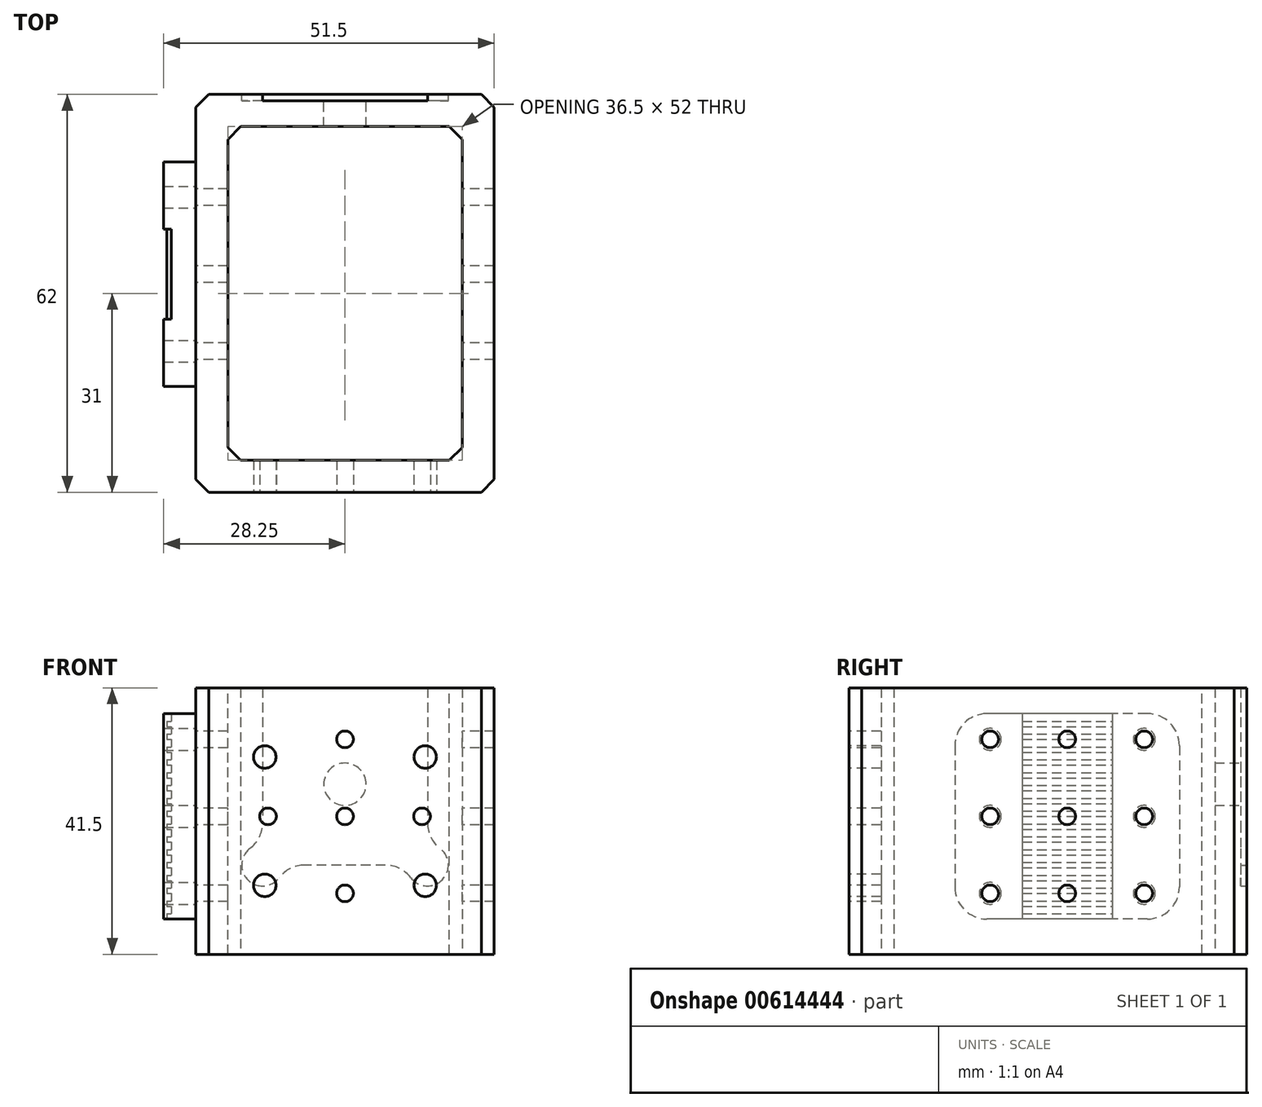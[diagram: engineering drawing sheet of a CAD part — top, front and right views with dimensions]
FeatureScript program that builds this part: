
annotation { "Feature Type Name" : "Feature", "Feature Type Description" : "" }
export const myFeature = defineFeature(function(context is Context, id is Id, definition is map)
    precondition{}
    {
        {
            var Q0;
            Q0=qCreatedBy(makeId("Top.planeOp"),FACE);
            var sketch = newSketch(context, id + "F0", { "sketchPlane" : qUnion([Q0])});
            skLineSegment(sketch, "E0.bottom", {"start": v(-18.25, 26) * mm, "end": v(18.25, 26) * mm});
            skLineSegment(sketch, "E0.top", {"start": v(-18.25, -26) * mm, "end": v(18.25, -26) * mm});
            skLineSegment(sketch, "E0.left", {"start": v(-18.25, 26) * mm, "end": v(-18.25, -26) * mm});
            skLineSegment(sketch, "E0.right", {"start": v(18.25, 26) * mm, "end": v(18.25, -26) * mm});
            skLineSegment(sketch, "E1.0", {"start": v(-23.25, 31) * mm, "end": v(-23.25, -31) * mm});
            skLineSegment(sketch, "E1.1", {"start": v(-23.25, 31) * mm, "end": v(23.25, 31) * mm});
            skLineSegment(sketch, "E1.2", {"start": v(23.25, 31) * mm, "end": v(23.25, -31) * mm});
            skLineSegment(sketch, "E1.3", {"start": v(-23.25, -31) * mm, "end": v(23.25, -31) * mm});
            skSolve(sketch);
        }
        {
            var Q0;
            Q0 = qSketchRegion(id + "F0", true);
            extrude(context, id + "F1", {"entities" : qUnion([Q0]), "depth" : 41.5 * mm, "offsetDistance" : 25 * mm});
        }
        {
            var Q0;
            Q0=makeQuery(id+"F1.opExtrude","SWEPT_EDGE",EDGE,{"disambiguationData":[OSD([sQuery(id+"F0.wireOp",EDGE,"E0.bottom"),sQuery(id+"F0.wireOp",EDGE,"E0.right")])]});
            var Q1;
            Q1=makeQuery(id+"F1.opExtrude","SWEPT_EDGE",EDGE,{"disambiguationData":[OSD([sQuery(id+"F0.wireOp",EDGE,"E0.bottom"),sQuery(id+"F0.wireOp",EDGE,"E0.left")])]});
            var Q2;
            Q2=makeQuery(id+"F1.opExtrude","SWEPT_EDGE",EDGE,{"disambiguationData":[OSD([sQuery(id+"F0.wireOp",EDGE,"E0.top"),sQuery(id+"F0.wireOp",EDGE,"E0.right")])]});
            var Q3;
            Q3=makeQuery(id+"F1.opExtrude","SWEPT_EDGE",EDGE,{"disambiguationData":[OSD([sQuery(id+"F0.wireOp",EDGE,"E0.top"),sQuery(id+"F0.wireOp",EDGE,"E0.left")])]});
            var Q4;
            Q4=makeQuery(id+"F1.opExtrude","SWEPT_EDGE",EDGE,{"disambiguationData":[OSD([sQuery(id+"F0.wireOp",EDGE,"E1.0"),sQuery(id+"F0.wireOp",EDGE,"E1.3")])]});
            var Q5;
            Q5=makeQuery(id+"F1.opExtrude","SWEPT_EDGE",EDGE,{"disambiguationData":[OSD([sQuery(id+"F0.wireOp",EDGE,"E1.2"),sQuery(id+"F0.wireOp",EDGE,"E1.3")])]});
            var Q6;
            Q6=makeQuery(id+"F1.opExtrude","SWEPT_EDGE",EDGE,{"disambiguationData":[OSD([sQuery(id+"F0.wireOp",EDGE,"E1.1"),sQuery(id+"F0.wireOp",EDGE,"E1.2")])]});
            var Q7;
            Q7=makeQuery(id+"F1.opExtrude","SWEPT_EDGE",EDGE,{"disambiguationData":[OSD([sQuery(id+"F0.wireOp",EDGE,"E1.0"),sQuery(id+"F0.wireOp",EDGE,"E1.1")])]});
            chamfer(context, id + "F2", {"entities" : qUnion([Q0, Q1, Q2, Q3, Q4, Q5, Q6, Q7]), "width" : 2 * mm, "tangentPropagation" : true});
        }
        {
            var Q0;
            Q0=makeQuery(id+"F1.opExtrude","SWEPT_FACE",FACE,{"disambiguationData":[OSD([sQuery(id+"F0.wireOp",EDGE,"E1.3")])]});
            var sketch = newSketch(context, id + "F3", { "sketchPlane" : qUnion([Q0])});
            skCircle(sketch, "E2", {"center": v(-12.5, 30.75) * mm, "radius": 1.75 * mm});
            skCircle(sketch, "E3", {"center": v(12.5, 30.75) * mm, "radius": 1.75 * mm});
            skCircle(sketch, "E4", {"center": v(-12.5, 10.75) * mm, "radius": 1.75 * mm});
            skCircle(sketch, "E5", {"center": v(12.5, 10.75) * mm, "radius": 1.75 * mm});
            skSolve(sketch);
        }
        {
            var Q0;
            Q0 = qSketchRegion(id + "F3", true);
            extrude(context, id + "F4", {"entities" : qUnion([Q0]), "operationType" : NewBodyOperationType.REMOVE, "oppositeDirection" : true, "depth" : 10 * mm, "offsetDistance" : 25 * mm});
        }
        {
            var Q0;
            Q0=makeQuery(id+"F1.opExtrude","SWEPT_FACE",FACE,{"disambiguationData":[OSD([sQuery(id+"F0.wireOp",EDGE,"E1.0")])]});
            var sketch = newSketch(context, id + "F5", { "sketchPlane" : qUnion([Q0])});
            skCircle(sketch, "E6", {"center": v(-3, 33.5) * mm, "radius": 1.3 * mm});
            skCircle(sketch, "E7", {"center": v(-3, 21.5) * mm, "radius": 1.3 * mm});
            skCircle(sketch, "E8", {"center": v(-3, 9.5) * mm, "radius": 1.3 * mm});
            skCircle(sketch, "E9", {"center": v(9, 21.5) * mm, "radius": 1.3 * mm});
            skCircle(sketch, "E10", {"center": v(-15, 21.5) * mm, "radius": 1.3 * mm});
            skCircle(sketch, "E11", {"center": v(-15, 33.5) * mm, "radius": 1.3 * mm});
            skCircle(sketch, "E12", {"center": v(9, 33.5) * mm, "radius": 1.3 * mm});
            skCircle(sketch, "E13", {"center": v(9, 9.5) * mm, "radius": 1.3 * mm});
            skCircle(sketch, "E14", {"center": v(-15, 9.5) * mm, "radius": 1.3 * mm});
            skSolve(sketch);
        }
        {
            var Q0;
            Q0 = qSketchRegion(id + "F5", true);
            extrude(context, id + "F6", {"entities" : qUnion([Q0]), "operationType" : NewBodyOperationType.REMOVE, "endBound" : BoundingType.THROUGH_ALL, "oppositeDirection" : true, "depth" : 25 * mm, "offsetDistance" : 25 * mm});
        }
        {
            var Q0;
            Q0=makeQuery(id+"F1.opExtrude","SWEPT_FACE",FACE,{"disambiguationData":[OSD([sQuery(id+"F0.wireOp",EDGE,"E1.1")])]});
            var sketch = newSketch(context, id + "F7", { "sketchPlane" : qUnion([Q0])});
            skCircle(sketch, "E15", {"center": v(0, 26.5) * mm, "radius": 3.3 * mm});
            skSolve(sketch);
        }
        {
            var Q0;
            Q0 = qSketchRegion(id + "F7", true);
            extrude(context, id + "F8", {"entities" : qUnion([Q0]), "operationType" : NewBodyOperationType.REMOVE, "oppositeDirection" : true, "depth" : 10 * mm, "offsetDistance" : 25 * mm});
        }
        {
            var Q0;
            Q0=makeQuery(id+"F1.opExtrude","SWEPT_FACE",FACE,{"disambiguationData":[OSD([sQuery(id+"F0.wireOp",EDGE,"E1.1")])]});
            var sketch = newSketch(context, id + "F9", { "sketchPlane" : qUnion([Q0])});
            skLineSegment(sketch, "E16.bottom", {"start": v(-12.85, 41.5) * mm, "end": v(12.85, 41.5) * mm});
            skLineSegment(sketch, "E16.top", {"start": v(-12.85, 13.9) * mm, "end": v(12.85, 13.9) * mm});
            skLineSegment(sketch, "E16.left", {"start": v(-12.85, 41.5) * mm, "end": v(-12.85, 13.9) * mm});
            skLineSegment(sketch, "E16.right", {"start": v(12.85, 41.5) * mm, "end": v(12.85, 13.9) * mm});
            skLineSegment(sketch, "E17", {"start": v(0, 26.5) * mm, "end": v(32.94, 26.5) * mm, "construction": true});
            skSolve(sketch);
        }
        {
            var Q0;
            Q0 = qSketchRegion(id + "F9", true);
            extrude(context, id + "F10", {"entities" : qUnion([Q0]), "operationType" : NewBodyOperationType.REMOVE, "oppositeDirection" : true, "depth" : 1 * mm, "offsetDistance" : 25 * mm});
        }
        {
            var Q0;
            Q0=makeQuery(id+"F1.opExtrude","SWEPT_FACE",FACE,{"disambiguationData":[OSD([sQuery(id+"F0.wireOp",EDGE,"E1.1")])]});
            var sketch = newSketch(context, id + "F11", { "sketchPlane" : qUnion([Q0])});
            skCircle(sketch, "E18", {"center": v(-12.85, 13.9) * mm, "radius": 3.25 * mm});
            skCircle(sketch, "E19", {"center": v(12.85, 13.9) * mm, "radius": 3.25 * mm});
            skSolve(sketch);
        }
        {
            var Q0;
            Q0 = qSketchRegion(id + "F11", true);
            var Q1;
            Q1=makeQuery(id+"F10.boolean.opBoolean","COPY",FACE,{"derivedFrom":makeQuery(id+"F10.opExtrude","CAP_FACE",FACE,{"disambiguationData":[OSD([sQuery(id+"F9.wireOp",EDGE,"E16.bottom"),sQuery(id+"F9.wireOp",EDGE,"E16.top"),sQuery(id+"F9.wireOp",EDGE,"E16.left"),sQuery(id+"F9.wireOp",EDGE,"E16.right")])],"isStart":false})});
            extrude(context, id + "F12", {"entities" : qUnion([Q0]), "operationType" : NewBodyOperationType.REMOVE, "endBound" : BoundingType.UP_TO_SURFACE, "oppositeDirection" : true, "depth" : 25 * mm, "endBoundEntityFace" : qUnion([Q1]), "offsetDistance" : 25 * mm});
        }
        {
            var Q0;
            Q0=makeQuery(id+"F12.boolean.opBoolean","INTERSECT",EDGE,{"derivedFrom":[makeQuery(id+"F10.boolean.opBoolean","COPY",FACE,{"derivedFrom":makeQuery(id+"F10.opExtrude","SWEPT_FACE",FACE,{"disambiguationData":[OSD([sQuery(id+"F9.wireOp",EDGE,"E16.left")])]})}),makeQuery(id+"F12.opExtrude","SWEPT_FACE",FACE,{"disambiguationData":[OSD([sQuery(id+"F11.wireOp",EDGE,"E18")])]})]});
            var Q1;
            Q1=makeQuery(id+"F12.boolean.opBoolean","INTERSECT",EDGE,{"derivedFrom":[makeQuery(id+"F10.boolean.opBoolean","COPY",FACE,{"derivedFrom":makeQuery(id+"F10.opExtrude","SWEPT_FACE",FACE,{"disambiguationData":[OSD([sQuery(id+"F9.wireOp",EDGE,"E16.right")])]})}),makeQuery(id+"F12.opExtrude","SWEPT_FACE",FACE,{"disambiguationData":[OSD([sQuery(id+"F11.wireOp",EDGE,"E19")])]})]});
            var Q2;
            Q2=makeQuery(id+"F12.boolean.opBoolean","INTERSECT",EDGE,{"derivedFrom":[makeQuery(id+"F10.boolean.opBoolean","COPY",FACE,{"derivedFrom":makeQuery(id+"F10.opExtrude","SWEPT_FACE",FACE,{"disambiguationData":[OSD([sQuery(id+"F9.wireOp",EDGE,"E16.top")])]})}),makeQuery(id+"F12.opExtrude","SWEPT_FACE",FACE,{"disambiguationData":[OSD([sQuery(id+"F11.wireOp",EDGE,"E19")])]})]});
            var Q3;
            Q3=makeQuery(id+"F12.boolean.opBoolean","INTERSECT",EDGE,{"derivedFrom":[makeQuery(id+"F10.boolean.opBoolean","COPY",FACE,{"derivedFrom":makeQuery(id+"F10.opExtrude","SWEPT_FACE",FACE,{"disambiguationData":[OSD([sQuery(id+"F9.wireOp",EDGE,"E16.top")])]})}),makeQuery(id+"F12.opExtrude","SWEPT_FACE",FACE,{"disambiguationData":[OSD([sQuery(id+"F11.wireOp",EDGE,"E18")])]})]});
            fillet(context, id + "F13", {"entities" : qUnion([Q0, Q1, Q2, Q3]), "radius" : 5 * mm, "tangentPropagation" : true, "allowEdgeOverflow" : false});
        }
        {
            var Q0;
            Q0=makeQuery(id+"F1.opExtrude","SWEPT_FACE",FACE,{"disambiguationData":[OSD([sQuery(id+"F0.wireOp",EDGE,"E1.3")])]});
            var sketch = newSketch(context, id + "F14", { "sketchPlane" : qUnion([Q0])});
            skCircle(sketch, "E20", {"center": v(0, 21.5) * mm, "radius": 1.3 * mm});
            skCircle(sketch, "E21", {"center": v(0, 9.5) * mm, "radius": 1.3 * mm});
            skCircle(sketch, "E22", {"center": v(0, 33.5) * mm, "radius": 1.3 * mm});
            skCircle(sketch, "E23", {"center": v(-12, 21.5) * mm, "radius": 1.3 * mm});
            skCircle(sketch, "E24", {"center": v(12, 21.5) * mm, "radius": 1.3 * mm});
            skSolve(sketch);
        }
        {
            var Q0;
            Q0 = qSketchRegion(id + "F14", true);
            extrude(context, id + "F15", {"entities" : qUnion([Q0]), "operationType" : NewBodyOperationType.REMOVE, "oppositeDirection" : true, "depth" : 10 * mm, "offsetDistance" : 25 * mm});
        }
        {
            var Q0;
            Q0=makeQuery(id+"F1.opExtrude","SWEPT_FACE",FACE,{"disambiguationData":[OSD([sQuery(id+"F0.wireOp",EDGE,"E1.0")])]});
            var sketch = newSketch(context, id + "F16", { "sketchPlane" : qUnion([Q0])});
            skLineSegment(sketch, "E25.bottom", {"start": v(-15.5, 37.5) * mm, "end": v(9.5, 37.5) * mm});
            skLineSegment(sketch, "E25.top", {"start": v(-15.5, 5.5) * mm, "end": v(9.5, 5.5) * mm});
            skLineSegment(sketch, "E25.left", {"start": v(-20.5, 32.5) * mm, "end": v(-20.5, 10.5) * mm});
            skLineSegment(sketch, "E25.right", {"start": v(14.5, 32.5) * mm, "end": v(14.5, 10.5) * mm});
            skLineSegment(sketch, "E26", {"start": v(-3, 33.5) * mm, "end": v(-3, 9.5) * mm, "construction": true});
            skLineSegment(sketch, "E27", {"start": v(-15, 21.5) * mm, "end": v(9, 21.5) * mm, "construction": true});
            skCircle(sketch, "E28", {"center": v(-15, 21.5) * mm, "radius": 1.7 * mm});
            skCircle(sketch, "E29", {"center": v(9, 21.5) * mm, "radius": 1.7 * mm});
            skCircle(sketch, "E30", {"center": v(-15, 33.5) * mm, "radius": 1.7 * mm});
            skCircle(sketch, "E31", {"center": v(9, 33.5) * mm, "radius": 1.7 * mm});
            skCircle(sketch, "E32", {"center": v(9, 9.5) * mm, "radius": 1.7 * mm});
            skCircle(sketch, "E33", {"center": v(-15, 9.5) * mm, "radius": 1.7 * mm});
            skPoint(sketch, "E34.visualSharp", {"position": v(-20.5, 37.5) * mm});
            skArc(sketch, "E34.filletArc", {"start": v(-15.5, 37.5) * mm, "mid": v(-19.04, 36.04) * mm, "end": v(-20.5, 32.5) * mm});
            skPoint(sketch, "E35.visualSharp", {"position": v(14.5, 37.5) * mm});
            skArc(sketch, "E35.filletArc", {"start": v(14.5, 32.5) * mm, "mid": v(13.04, 36.04) * mm, "end": v(9.5, 37.5) * mm});
            skPoint(sketch, "E36.visualSharp", {"position": v(14.5, 5.5) * mm});
            skArc(sketch, "E36.filletArc", {"start": v(9.5, 5.5) * mm, "mid": v(13.04, 6.96) * mm, "end": v(14.5, 10.5) * mm});
            skPoint(sketch, "E37.visualSharp", {"position": v(-20.5, 5.5) * mm});
            skArc(sketch, "E37.filletArc", {"start": v(-20.5, 10.5) * mm, "mid": v(-19.04, 6.96) * mm, "end": v(-15.5, 5.5) * mm});
            skSolve(sketch);
        }
        {
            var Q0;
            Q0 = qSketchRegion(id + "F16", true);
            extrude(context, id + "F17", {"entities" : qUnion([Q0]), "depth" : 5 * mm, "offsetDistance" : 25 * mm});
        }
        {
            var Q0;
            Q0=makeQuery(id+"F17.opExtrude","CAP_FACE",FACE,{"disambiguationData":[OSD([sQuery(id+"F16.wireOp",EDGE,"E25.bottom"),sQuery(id+"F16.wireOp",EDGE,"E25.top"),sQuery(id+"F16.wireOp",EDGE,"E25.left"),sQuery(id+"F16.wireOp",EDGE,"E25.right"),sQuery(id+"F16.wireOp",EDGE,"E28"),sQuery(id+"F16.wireOp",EDGE,"E29"),sQuery(id+"F16.wireOp",EDGE,"E30"),sQuery(id+"F16.wireOp",EDGE,"E31"),sQuery(id+"F16.wireOp",EDGE,"E32"),sQuery(id+"F16.wireOp",EDGE,"E33"),sQuery(id+"F16.wireOp",EDGE,"E34.filletArc"),sQuery(id+"F16.wireOp",EDGE,"E35.filletArc"),sQuery(id+"F16.wireOp",EDGE,"E36.filletArc"),sQuery(id+"F16.wireOp",EDGE,"E37.filletArc")])],"isStart":false});
            var sketch = newSketch(context, id + "F18", { "sketchPlane" : qUnion([Q0])});
            skLineSegment(sketch, "E38.bottom", {"start": v(-10, 37.5) * mm, "end": v(4, 37.5) * mm});
            skLineSegment(sketch, "E38.top", {"start": v(-10, 5.5) * mm, "end": v(4, 5.5) * mm});
            skLineSegment(sketch, "E38.left", {"start": v(-10, 37.5) * mm, "end": v(-10, 5.5) * mm});
            skLineSegment(sketch, "E38.right", {"start": v(4, 37.5) * mm, "end": v(4, 5.5) * mm});
            skLineSegment(sketch, "E39", {"start": v(-15, 21.5) * mm, "end": v(9, 21.5) * mm, "construction": true});
            skLineSegment(sketch, "E40", {"start": v(-3, 21.5) * mm, "end": v(-3, 47.13) * mm, "construction": true});
            skSolve(sketch);
        }
        {
            var Q0;
            Q0 = qSketchRegion(id + "F18", true);
            extrude(context, id + "F19", {"entities" : qUnion([Q0]), "operationType" : NewBodyOperationType.REMOVE, "oppositeDirection" : true, "depth" : 1.2 * mm, "offsetDistance" : 25 * mm});
        }
        {
            var Q0;
            Q0=makeQuery(id+"F19.boolean.opBoolean","COPY",FACE,{"derivedFrom":makeQuery(id+"F19.opExtrude","CAP_FACE",FACE,{"disambiguationData":[OSD([sQuery(id+"F18.wireOp",EDGE,"E38.bottom"),sQuery(id+"F18.wireOp",EDGE,"E38.top"),sQuery(id+"F18.wireOp",EDGE,"E38.left"),sQuery(id+"F18.wireOp",EDGE,"E38.right")])],"isStart":false})});
            var sketch = newSketch(context, id + "F20", { "sketchPlane" : qUnion([Q0])});
            skLineSegment(sketch, "E41.bottom", {"start": v(4, 5.5) * mm, "end": v(-10, 5.5) * mm});
            skLineSegment(sketch, "E41.top", {"start": v(4, 6.3) * mm, "end": v(-10, 6.3) * mm});
            skLineSegment(sketch, "E41.left", {"start": v(4, 5.5) * mm, "end": v(4, 6.3) * mm});
            skLineSegment(sketch, "E41.right", {"start": v(-10, 5.5) * mm, "end": v(-10, 6.3) * mm});
            skLineSegment(sketch, "E42.0.1.0", {"start": v(4, 7.5) * mm, "end": v(-10, 7.5) * mm});
            skLineSegment(sketch, "E42.0.1.1", {"start": v(4, 8.3) * mm, "end": v(-10, 8.3) * mm});
            skLineSegment(sketch, "E42.0.1.2", {"start": v(4, 7.5) * mm, "end": v(4, 8.3) * mm});
            skLineSegment(sketch, "E42.0.1.3", {"start": v(-10, 7.5) * mm, "end": v(-10, 8.3) * mm});
            skLineSegment(sketch, "E42.0.2.0", {"start": v(4, 9.5) * mm, "end": v(-10, 9.5) * mm});
            skLineSegment(sketch, "E42.0.2.1", {"start": v(4, 10.3) * mm, "end": v(-10, 10.3) * mm});
            skLineSegment(sketch, "E42.0.2.2", {"start": v(4, 9.5) * mm, "end": v(4, 10.3) * mm});
            skLineSegment(sketch, "E42.0.2.3", {"start": v(-10, 9.5) * mm, "end": v(-10, 10.3) * mm});
            skLineSegment(sketch, "E42.0.3.0", {"start": v(4, 11.5) * mm, "end": v(-10, 11.5) * mm});
            skLineSegment(sketch, "E42.0.3.1", {"start": v(4, 12.3) * mm, "end": v(-10, 12.3) * mm});
            skLineSegment(sketch, "E42.0.3.2", {"start": v(4, 11.5) * mm, "end": v(4, 12.3) * mm});
            skLineSegment(sketch, "E42.0.3.3", {"start": v(-10, 11.5) * mm, "end": v(-10, 12.3) * mm});
            skLineSegment(sketch, "E42.0.4.0", {"start": v(4, 13.5) * mm, "end": v(-10, 13.5) * mm});
            skLineSegment(sketch, "E42.0.4.1", {"start": v(4, 14.3) * mm, "end": v(-10, 14.3) * mm});
            skLineSegment(sketch, "E42.0.4.2", {"start": v(4, 13.5) * mm, "end": v(4, 14.3) * mm});
            skLineSegment(sketch, "E42.0.4.3", {"start": v(-10, 13.5) * mm, "end": v(-10, 14.3) * mm});
            skLineSegment(sketch, "E42.0.5.0", {"start": v(4, 15.5) * mm, "end": v(-10, 15.5) * mm});
            skLineSegment(sketch, "E42.0.5.1", {"start": v(4, 16.3) * mm, "end": v(-10, 16.3) * mm});
            skLineSegment(sketch, "E42.0.5.2", {"start": v(4, 15.5) * mm, "end": v(4, 16.3) * mm});
            skLineSegment(sketch, "E42.0.5.3", {"start": v(-10, 15.5) * mm, "end": v(-10, 16.3) * mm});
            skLineSegment(sketch, "E42.0.6.0", {"start": v(4, 17.5) * mm, "end": v(-10, 17.5) * mm});
            skLineSegment(sketch, "E42.0.6.1", {"start": v(4, 18.3) * mm, "end": v(-10, 18.3) * mm});
            skLineSegment(sketch, "E42.0.6.2", {"start": v(4, 17.5) * mm, "end": v(4, 18.3) * mm});
            skLineSegment(sketch, "E42.0.6.3", {"start": v(-10, 17.5) * mm, "end": v(-10, 18.3) * mm});
            skLineSegment(sketch, "E42.0.7.0", {"start": v(4, 19.5) * mm, "end": v(-10, 19.5) * mm});
            skLineSegment(sketch, "E42.0.7.1", {"start": v(4, 20.3) * mm, "end": v(-10, 20.3) * mm});
            skLineSegment(sketch, "E42.0.7.2", {"start": v(4, 19.5) * mm, "end": v(4, 20.3) * mm});
            skLineSegment(sketch, "E42.0.7.3", {"start": v(-10, 19.5) * mm, "end": v(-10, 20.3) * mm});
            skLineSegment(sketch, "E42.0.8.0", {"start": v(4, 21.5) * mm, "end": v(-10, 21.5) * mm});
            skLineSegment(sketch, "E42.0.8.1", {"start": v(4, 22.3) * mm, "end": v(-10, 22.3) * mm});
            skLineSegment(sketch, "E42.0.8.2", {"start": v(4, 21.5) * mm, "end": v(4, 22.3) * mm});
            skLineSegment(sketch, "E42.0.8.3", {"start": v(-10, 21.5) * mm, "end": v(-10, 22.3) * mm});
            skLineSegment(sketch, "E42.0.9.0", {"start": v(4, 23.5) * mm, "end": v(-10, 23.5) * mm});
            skLineSegment(sketch, "E42.0.9.1", {"start": v(4, 24.3) * mm, "end": v(-10, 24.3) * mm});
            skLineSegment(sketch, "E42.0.9.2", {"start": v(4, 23.5) * mm, "end": v(4, 24.3) * mm});
            skLineSegment(sketch, "E42.0.9.3", {"start": v(-10, 23.5) * mm, "end": v(-10, 24.3) * mm});
            skLineSegment(sketch, "E42.0.10.0", {"start": v(4, 25.5) * mm, "end": v(-10, 25.5) * mm});
            skLineSegment(sketch, "E42.0.10.1", {"start": v(4, 26.3) * mm, "end": v(-10, 26.3) * mm});
            skLineSegment(sketch, "E42.0.10.2", {"start": v(4, 25.5) * mm, "end": v(4, 26.3) * mm});
            skLineSegment(sketch, "E42.0.10.3", {"start": v(-10, 25.5) * mm, "end": v(-10, 26.3) * mm});
            skLineSegment(sketch, "E42.0.11.0", {"start": v(4, 27.5) * mm, "end": v(-10, 27.5) * mm});
            skLineSegment(sketch, "E42.0.11.1", {"start": v(4, 28.3) * mm, "end": v(-10, 28.3) * mm});
            skLineSegment(sketch, "E42.0.11.2", {"start": v(4, 27.5) * mm, "end": v(4, 28.3) * mm});
            skLineSegment(sketch, "E42.0.11.3", {"start": v(-10, 27.5) * mm, "end": v(-10, 28.3) * mm});
            skLineSegment(sketch, "E42.0.12.0", {"start": v(4, 29.5) * mm, "end": v(-10, 29.5) * mm});
            skLineSegment(sketch, "E42.0.12.1", {"start": v(4, 30.3) * mm, "end": v(-10, 30.3) * mm});
            skLineSegment(sketch, "E42.0.12.2", {"start": v(4, 29.5) * mm, "end": v(4, 30.3) * mm});
            skLineSegment(sketch, "E42.0.12.3", {"start": v(-10, 29.5) * mm, "end": v(-10, 30.3) * mm});
            skLineSegment(sketch, "E42.0.13.0", {"start": v(4, 31.5) * mm, "end": v(-10, 31.5) * mm});
            skLineSegment(sketch, "E42.0.13.1", {"start": v(4, 32.3) * mm, "end": v(-10, 32.3) * mm});
            skLineSegment(sketch, "E42.0.13.2", {"start": v(4, 31.5) * mm, "end": v(4, 32.3) * mm});
            skLineSegment(sketch, "E42.0.13.3", {"start": v(-10, 31.5) * mm, "end": v(-10, 32.3) * mm});
            skLineSegment(sketch, "E42.0.14.0", {"start": v(4, 33.5) * mm, "end": v(-10, 33.5) * mm});
            skLineSegment(sketch, "E42.0.14.1", {"start": v(4, 34.3) * mm, "end": v(-10, 34.3) * mm});
            skLineSegment(sketch, "E42.0.14.2", {"start": v(4, 33.5) * mm, "end": v(4, 34.3) * mm});
            skLineSegment(sketch, "E42.0.14.3", {"start": v(-10, 33.5) * mm, "end": v(-10, 34.3) * mm});
            skLineSegment(sketch, "E42.0.15.0", {"start": v(4, 35.5) * mm, "end": v(-10, 35.5) * mm});
            skLineSegment(sketch, "E42.0.15.1", {"start": v(4, 36.3) * mm, "end": v(-10, 36.3) * mm});
            skLineSegment(sketch, "E42.0.15.2", {"start": v(4, 35.5) * mm, "end": v(4, 36.3) * mm});
            skLineSegment(sketch, "E42.0.15.3", {"start": v(-10, 35.5) * mm, "end": v(-10, 36.3) * mm});
            skLineSegment(sketch, "E42.direction1", {"start": v(-10, 5.5) * mm, "end": v(15, 5.5) * mm, "construction": true});
            skLineSegment(sketch, "E42.direction2", {"start": v(-10, 5.5) * mm, "end": v(-10, 7.5) * mm, "construction": true});
            skSolve(sketch);
        }
        {
            var Q0;
            Q0 = qSketchRegion(id + "F20", true);
            extrude(context, id + "F21", {"entities" : qUnion([Q0]), "operationType" : NewBodyOperationType.ADD, "depth" : .7 * mm, "offsetDistance" : 25 * mm});
        }
    });
